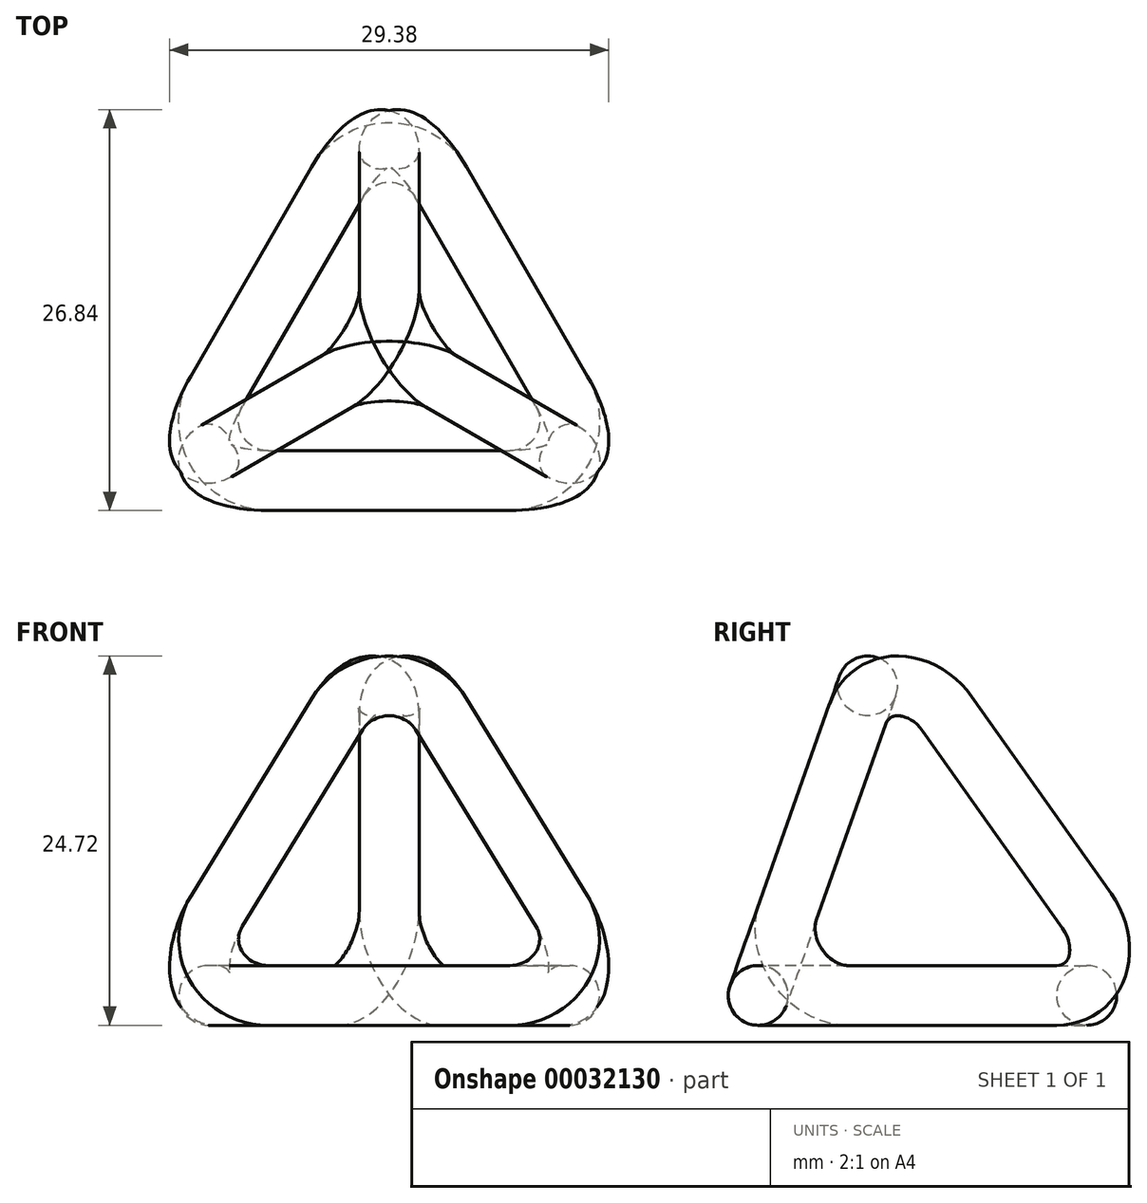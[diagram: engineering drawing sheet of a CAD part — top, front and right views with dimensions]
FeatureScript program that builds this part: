
annotation { "Feature Type Name" : "Feature", "Feature Type Description" : "" }
export const myFeature = defineFeature(function(context is Context, id is Id, definition is map)
    precondition{}
    {
        {
            var Q0;
            Q0=qCreatedBy(makeId("Top.planeOp"),FACE);
            var sketch = newSketch(context, id + "F0", { "sketchPlane" : qUnion([Q0])});
            skLineSegment(sketch, "E0", {"start": v(-3.46, 9.44) * mm, "end": v(-11.54, -4.54) * mm});
            skLineSegment(sketch, "E1", {"start": v(11.54, -4.54) * mm, "end": v(3.46, 9.44) * mm});
            skPoint(sketch, "E2.visualSharp", {"position": v(0, 15.44) * mm});
            skArc(sketch, "E2.filletArc", {"start": v(3.46, 9.44) * mm, "mid": v(0, 11.44) * mm, "end": v(-3.46, 9.44) * mm});
            skPoint(sketch, "E3.visualSharp", {"position": v(15, -10.54) * mm});
            skArc(sketch, "E3.filletArc", {"start": v(8.07, -10.54) * mm, "mid": v(11.54, -8.54) * mm, "end": v(11.54, -4.54) * mm});
            skPoint(sketch, "E4.visualSharp", {"position": v(-15, -10.54) * mm});
            skArc(sketch, "E4.filletArc", {"start": v(-11.54, -4.54) * mm, "mid": v(-11.54, -8.54) * mm, "end": v(-8.07, -10.54) * mm});
            skLineSegment(sketch, "E5", {"start": v(0, 15.44) * mm, "end": v(0, -10.54) * mm});
            skLineSegment(sketch, "E6", {"start": v(-15, -10.54) * mm, "end": v(7.5, 2.45) * mm});
            skLineSegment(sketch, "E7", {"start": v(15, -10.54) * mm, "end": v(-7.5, 2.45) * mm});
            skPoint(sketch, "E8", {"position": v(0, -1.88) * mm});
            skLineSegment(sketch, "E9", {"start": v(0, -1.88) * mm, "end": v(-15.28, -1.88) * mm});
            skLineSegment(sketch, "E10", {"start": v(8.07, -10.54) * mm, "end": v(0, -10.54) * mm});
            skLineSegment(sketch, "E11", {"start": v(0, -10.54) * mm, "end": v(-8.07, -10.54) * mm});
            skSolve(sketch);
        }
        {
            var Q0;
            Q0=qCreatedBy(makeId("Right.planeOp"),FACE);
            var sketch = newSketch(context, id + "F1", { "sketchPlane" : qUnion([Q0])});
            skLineSegment(sketch, "E12.1", {"start": v(15.44, 0) * mm, "end": v(-10.54, 0) * mm});
            skCircle(sketch, "E13", {"center": v(-10.54, 0) * mm, "radius": 2 * mm});
            skLineSegment(sketch, "E14", {"start": v(-1.88, 0) * mm, "end": v(-1.88, 18.08) * mm});
            skLineSegment(sketch, "E15", {"start": v(-10.54, 0) * mm, "end": v(-1.88, 24.5) * mm});
            skSolve(sketch);
        }
        {
            var Q0;
            {var subQ0=sQuery(id+"F1.wireOp",EDGE,"E15");var subQ3=sQuery(id+"F1.wireOp",EDGE,"E12.1");var subQ4=makeQuery(id+"F1.imprint","INTERSECT",VERTEX,{"derivedFrom":[subQ3,subQ0]});Q0=makeQuery(id+"F1.imprint","IMPRINT",FACE,{"disambiguationData":[TD([[makeQuery(id+"F1.imprint","IMPRINT",EDGE,{"disambiguationData":[TD([[subQ4,1.0]])],"derivedFrom":subQ3}),-1.0]])]});}
            var Q1;
            {var subQ0=sQuery(id+"F1.wireOp",EDGE,"E15");var subQ3=sQuery(id+"F1.wireOp",EDGE,"E12.1");var subQ4=makeQuery(id+"F1.imprint","INTERSECT",VERTEX,{"derivedFrom":[subQ3,subQ0]});Q1=makeQuery(id+"F1.imprint","IMPRINT",FACE,{"disambiguationData":[TD([[makeQuery(id+"F1.imprint","IMPRINT",EDGE,{"disambiguationData":[TD([[subQ4,1.0]])],"derivedFrom":subQ3}),1.0]])]});}
            var Q2;
            Q2=sQuery(id+"F0.wireOp",EDGE,"E11");
            var Q3;
            Q3=sQuery(id+"F0.wireOp",EDGE,"E4.filletArc");
            var Q4;
            Q4=sQuery(id+"F0.wireOp",EDGE,"E0");
            var Q5;
            Q5=sQuery(id+"F0.wireOp",EDGE,"E2.filletArc");
            var Q6;
            Q6=sQuery(id+"F0.wireOp",EDGE,"E1");
            var Q7;
            Q7=sQuery(id+"F0.wireOp",EDGE,"E3.filletArc");
            var Q8;
            Q8=sQuery(id+"F0.wireOp",EDGE,"E10");
            sweep(context, id + "F2", {"profiles" : qUnion([Q0, Q1]), "path" : qUnion([Q2, Q3, Q4, Q5, Q6, Q7, Q8])});
        }
        {
            var Q0;
            Q0=makeQuery(id+"F2.opSweep","SWEPT_BODY",BODY,{"disambiguationData":[OSD([sQuery(id+"F0.wireOp",EDGE,"E10"),sQuery(id+"F1.wireOp",EDGE,"E13")])]});
            var Q1;
            Q1=sQuery(id+"F0.wireOp",EDGE,"E11");
            transform(context, id + "F3", {"entities" : qUnion([Q0]), "transformType" : TransformType.ROTATION, "transformAxis" : qUnion([Q1]), "angle" : 70.53 * degree, "oppositeDirection" : true, "makeCopy" : true});
        }
        {
            var Q0;
            Q0=makeQuery(id+"F3.opPattern","COPY",BODY,{"derivedFrom":makeQuery(id+"F2.opSweep","SWEPT_BODY",BODY,{"disambiguationData":[OSD([sQuery(id+"F0.wireOp",EDGE,"E10"),sQuery(id+"F1.wireOp",EDGE,"E13")])]}),"instanceName":"1"});
            var Q1;
            Q1=sQuery(id+"F1.wireOp",EDGE,"E14");
            circularPattern(context, id + "F4", {"entities" : qUnion([Q0]), "axis" : qUnion([Q1]), "angle" : 360 * degree, "instanceCount" : 3, "equalSpace" : true});
        }
    });
